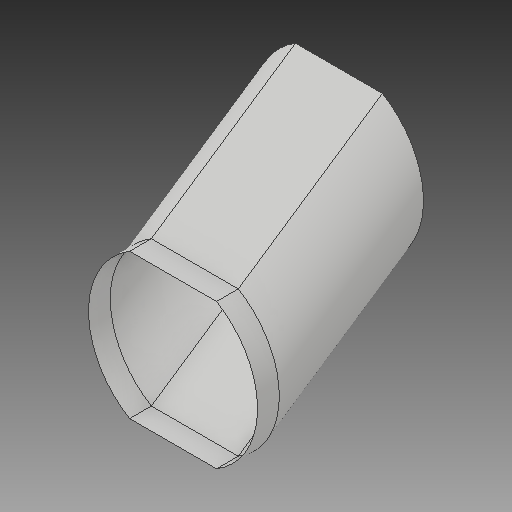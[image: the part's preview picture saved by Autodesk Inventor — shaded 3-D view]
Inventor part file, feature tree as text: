
AUTODESK INVENTOR PART (.ipt)
format: ipt  version: 2017 (Build 210142000, 142)  size: 138,240 bytes
history: native  units: in
note: dims shown in document units (in); Inventor stores cm internally (conversion verified against a paired STEP export)
features: sketch x2, plane x1, sweep x1, extrude x1, delete_face x1
ambient origin geometry x8: Origin, YZ Plane, XZ Plane, XY Plane, X Axis, Y Axis, Z Axis, Center Point
bodies: Solid1 (feature_tree)
feature tree (6):
  sketch  "Sketch1"  dims[d0=6.6667in d28=8.0in]
  plane  "Work Plane2"
  sweep  "ramp"
  extrude  "connection bottom"  Depth=3.8873in TaperAngle=0.0deg
  delete_face  "Delete Face1"
  sketch  "Sketch6"  dims[d30=0.0in d31=0.0in d32=1.0in d33=0.0in d62=0.8521in d110=4.0in d112=3.8873in d113=3.8873in d117=1.6458in d123=3.3333in d125=4.0in d127=3.8873in d128=3.8873in d132=1.6458in d138=3.3333in]
